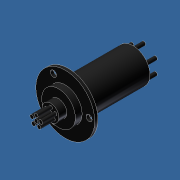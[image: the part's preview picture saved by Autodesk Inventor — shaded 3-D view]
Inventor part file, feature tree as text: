
AUTODESK INVENTOR PART (.ipt)
format: ipt  version: unknown  size: 240,128 bytes
history: native  units: in
note: dims shown in document units (in); Inventor stores cm internally (conversion verified against a paired STEP export)
features: extrude x7, sketch x7
ambient origin geometry x8: Origin, YZ Plane, XZ Plane, XY Plane, X Axis, Y Axis, Z Axis, Center Point
bodies: Solid1 (feature_tree)
feature tree (14):
  extrude  "Extrusion1"  Depth=0.1122in TaperAngle=0.0deg
  extrude  "Extrusion2"  Depth=0.2362in TaperAngle=0.0deg
  extrude  "Extrusion3"  Depth=0.2756in TaperAngle=0.0deg
  extrude  "Extrusion4"  Depth=0.128in
  extrude  "Extrusion5"  Depth=0.128in
  extrude  "Extrusion6"  Depth=1.1811in
  extrude  "Extrusion7"  Depth=0.128in
  sketch  "Sketch1"  dims[d0=2.0472in d1=0.1122in d2=0.0in]
  sketch  "Sketch2"  dims[d3=1.1713in d4=0.2362in d5=0.0in]
  sketch  "Sketch3"  dims[d6=0.5807in d7=0.2756in d8=0.0in]
  sketch  "Sketch4"  dims[d9=0.165in d10=0.128in]
  sketch  "Sketch5"  dims[d11=1.9685in d13=360.0deg d15=0.128in]
  sketch  "Sketch6"  dims[d16=0.5in d17=0.0in d18=1.1811in]
  sketch  "Sketch7"  dims[d19=2.2441in d20=0.0in d21=0.128in d22=0.4724in d23=2.3622in d25=360.0deg d27=0.375in d28=0.0in d29=1.6535in d30=0.2126in d31=1.1811in d33=360.0deg d35=0.375in d36=0.0in]
